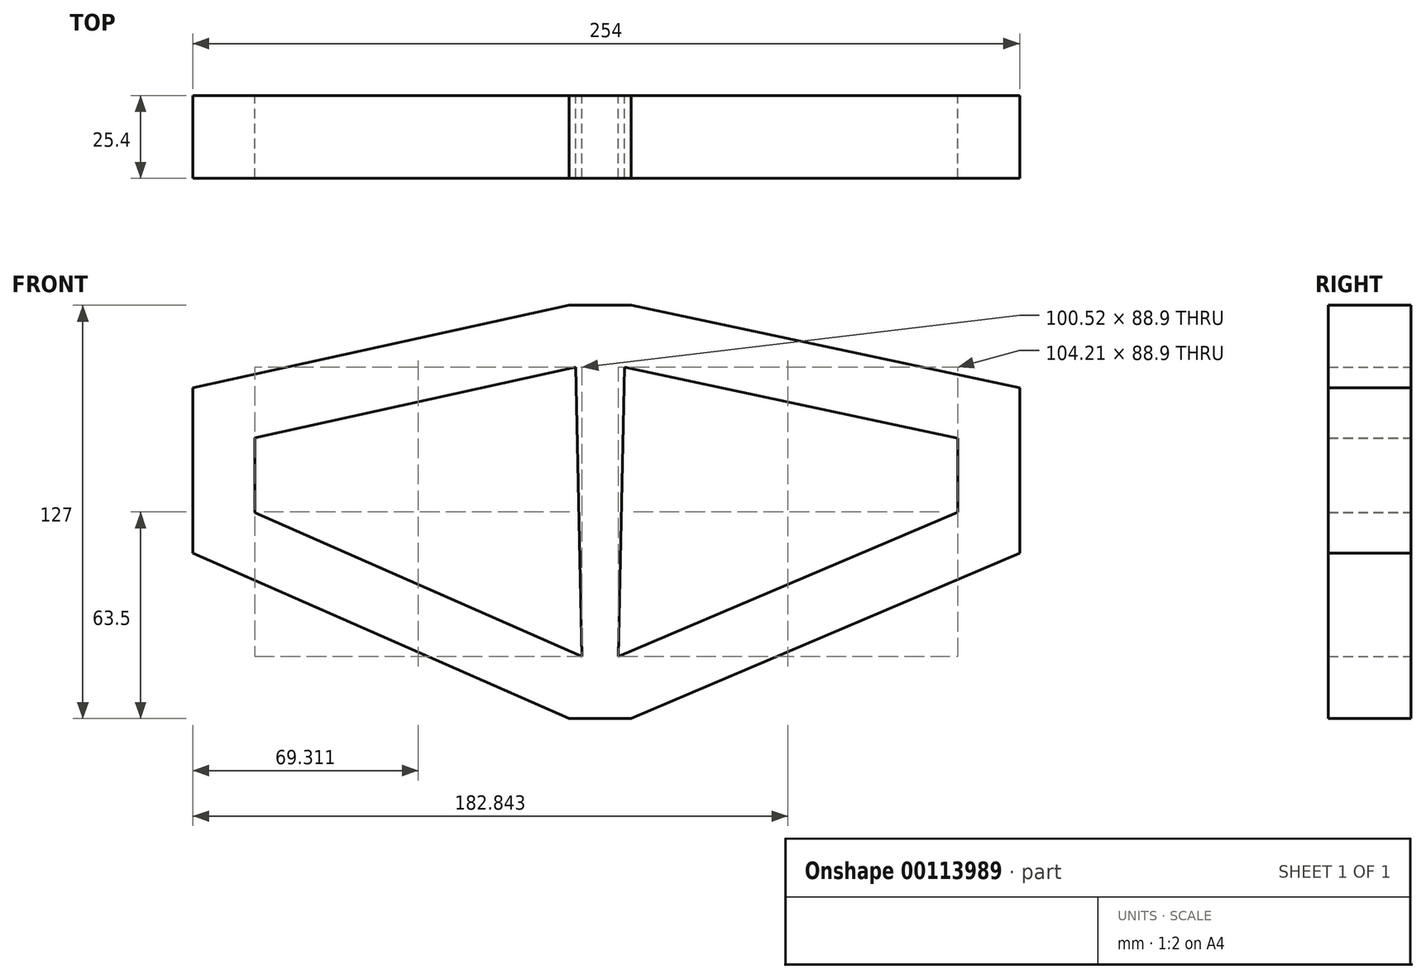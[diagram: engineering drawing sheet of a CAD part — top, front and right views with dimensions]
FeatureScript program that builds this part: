
annotation { "Feature Type Name" : "Feature", "Feature Type Description" : "" }
export const myFeature = defineFeature(function(context is Context, id is Id, definition is map)
    precondition{}
    {
        {
            var Q0;
            Q0=qCreatedBy(makeId("Front.planeOp"),FACE);
            var sketch = newSketch(context, id + "F0", { "sketchPlane" : qUnion([Q0])});
            skLineSegment(sketch, "E0", {"start": v(0, 0) * mm, "end": v(0, 50.8) * mm});
            skLineSegment(sketch, "E1", {"start": v(0, 0) * mm, "end": v(-119.38, -50.8) * mm});
            skLineSegment(sketch, "E2", {"start": v(-119.38, -50.8) * mm, "end": v(-138.43, -50.8) * mm});
            skLineSegment(sketch, "E3", {"start": v(-138.43, -50.8) * mm, "end": v(-254, 0) * mm});
            skLineSegment(sketch, "E4", {"start": v(-254, 0) * mm, "end": v(-254, 50.8) * mm});
            skLineSegment(sketch, "E5", {"start": v(-254, 50.8) * mm, "end": v(-138.43, 76.2) * mm});
            skLineSegment(sketch, "E6", {"start": v(-138.43, 76.2) * mm, "end": v(-119.38, 76.2) * mm});
            skLineSegment(sketch, "E7", {"start": v(-119.38, 76.2) * mm, "end": v(0, 50.8) * mm});
            skLineSegment(sketch, "E8.0", {"start": v(-234.95, 12.44) * mm, "end": v(-234.95, 35.48) * mm});
            skLineSegment(sketch, "E8.1", {"start": v(-134.43, -31.75) * mm, "end": v(-234.95, 12.44) * mm});
            skLineSegment(sketch, "E8.2", {"start": v(-234.95, 35.48) * mm, "end": v(-136.36, 57.15) * mm});
            skLineSegment(sketch, "E8.5", {"start": v(-121.38, 57.15) * mm, "end": v(-19.05, 35.38) * mm});
            skLineSegment(sketch, "E8.6", {"start": v(-19.05, 12.6) * mm, "end": v(-19.05, 35.38) * mm});
            skLineSegment(sketch, "E8.7", {"start": v(-19.05, 12.6) * mm, "end": v(-123.26, -31.75) * mm});
            skLineSegment(sketch, "E9", {"start": v(-136.36, 57.15) * mm, "end": v(-134.43, -31.75) * mm});
            skLineSegment(sketch, "E10", {"start": v(-121.38, 57.15) * mm, "end": v(-123.26, -31.75) * mm});
            skSolve(sketch);
        }
        {
            var Q0;
            Q0=makeQuery(id+"F0.imprint","IMPRINT",FACE,{"disambiguationData":[TD([[makeQuery(id+"F0.imprint","IMPRINT",EDGE,{"derivedFrom":sQuery(id+"F0.wireOp",EDGE,"E0")}),1.0]])]});
            extrude(context, id + "F1", {"entities" : qUnion([Q0]), "depth" : 25.4 * mm});
        }
    });
